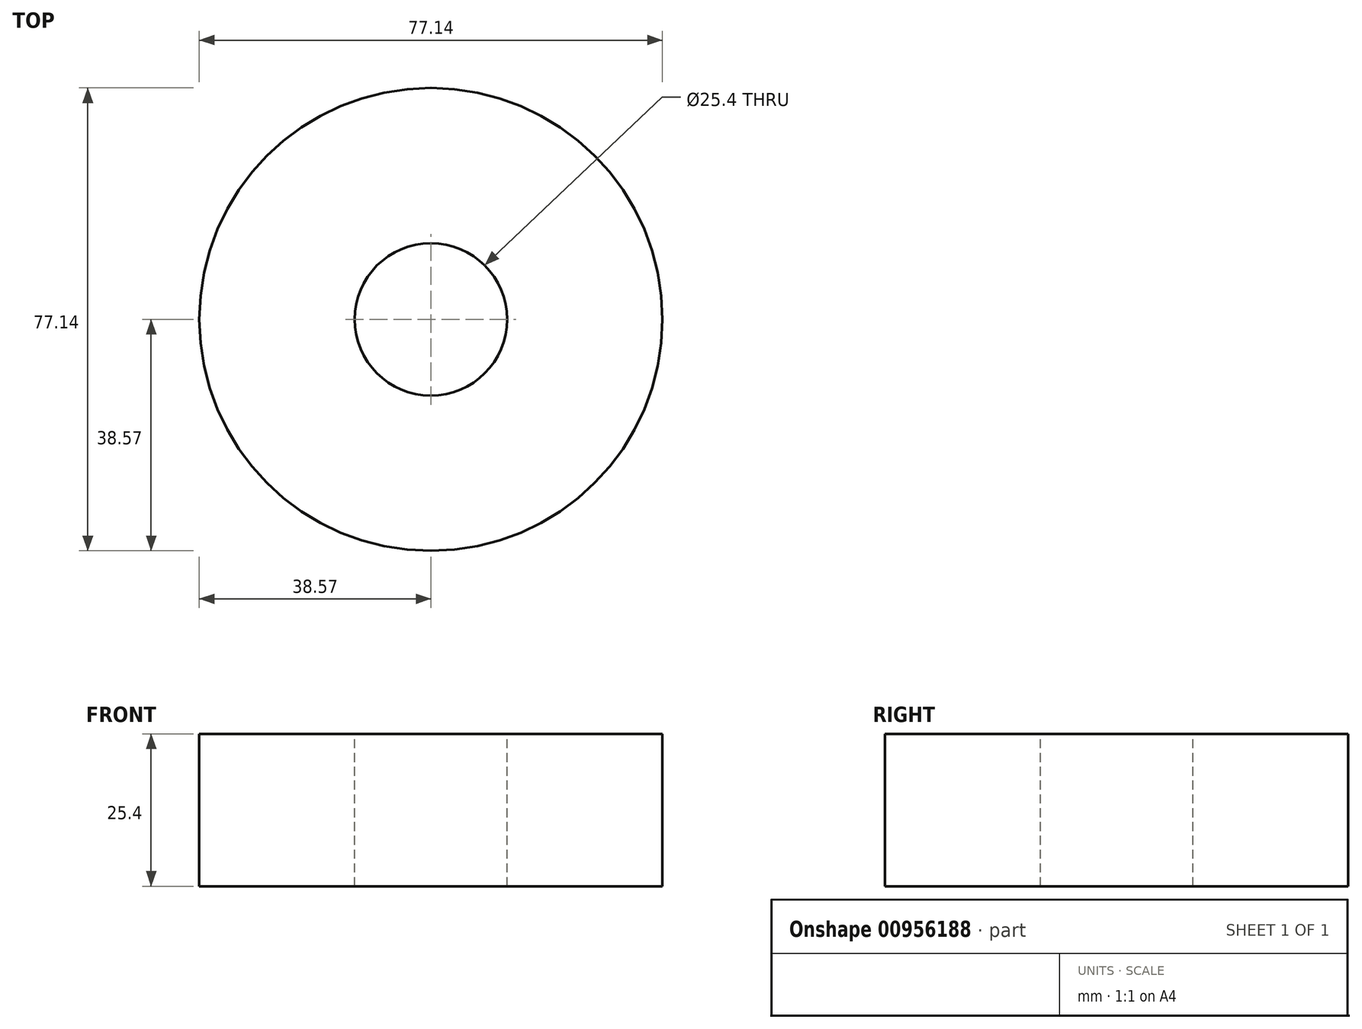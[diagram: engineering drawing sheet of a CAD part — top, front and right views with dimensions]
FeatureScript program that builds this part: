
annotation { "Feature Type Name" : "Feature", "Feature Type Description" : "" }
export const myFeature = defineFeature(function(context is Context, id is Id, definition is map)
    precondition{}
    {
        {
            var Q0;
            Q0=qCreatedBy(makeId("Top.planeOp"),FACE);
            var sketch = newSketch(context, id + "F0", { "sketchPlane" : qUnion([Q0])});
            skCircle(sketch, "E0", {"center": v(0, 0) * mm, "radius": 38.57 * mm});
            skPoint(sketch, "E1.center.orphan", {"position": v(75.7, 0) * mm});
            skSolve(sketch);
        }
        {
            var Q0;
            Q0=makeQuery(id+"F0.imprint","IMPRINT",FACE,{"disambiguationData":[TD([[makeQuery(id+"F0.imprint","IMPRINT",EDGE,{"derivedFrom":sQuery(id+"F0.wireOp",EDGE,"E0")}),1.0]])]});
            extrude(context, id + "F1", {"entities" : qUnion([Q0]), "depth" : 25.4 * mm, "offsetDistance" : 25.4 * mm});
        }
        {
            var Q0;
            Q0=makeQuery(id+"F1.opExtrude","CAP_FACE",FACE,{"disambiguationData":[OSD([sQuery(id+"F0.wireOp",EDGE,"E0")])],"isStart":false});
            var sketch = newSketch(context, id + "F2", { "sketchPlane" : qUnion([Q0])});
            skCircle(sketch, "E2", {"center": v(0, 0) * mm, "radius": 11.04 * mm});
            skSolve(sketch);
        }
        {
            var Q0;
            Q0=sQuery(id+"F2.wireOp",VERTEX,"E2.center");
            var Q1;
            Q1=makeQuery(id+"F1.opExtrude","SWEPT_BODY",BODY,{"disambiguationData":[OSD([sQuery(id+"F0.wireOp",EDGE,"E0")])]});
            hole(context, id + "F3", {"style" : HoleStyle.SIMPLE, "endStyle" : HoleEndStyle.THROUGH, "holeDiameter" : 25.4 * mm, "majorDiameter" : 6.35 * mm, "isTappedThrough" : true, "tappedDepth" : 12.7 * mm, "tapClearance" : 3, "locations" : qUnion([Q0]), "scope" : qUnion([Q1])});
        }
    });
